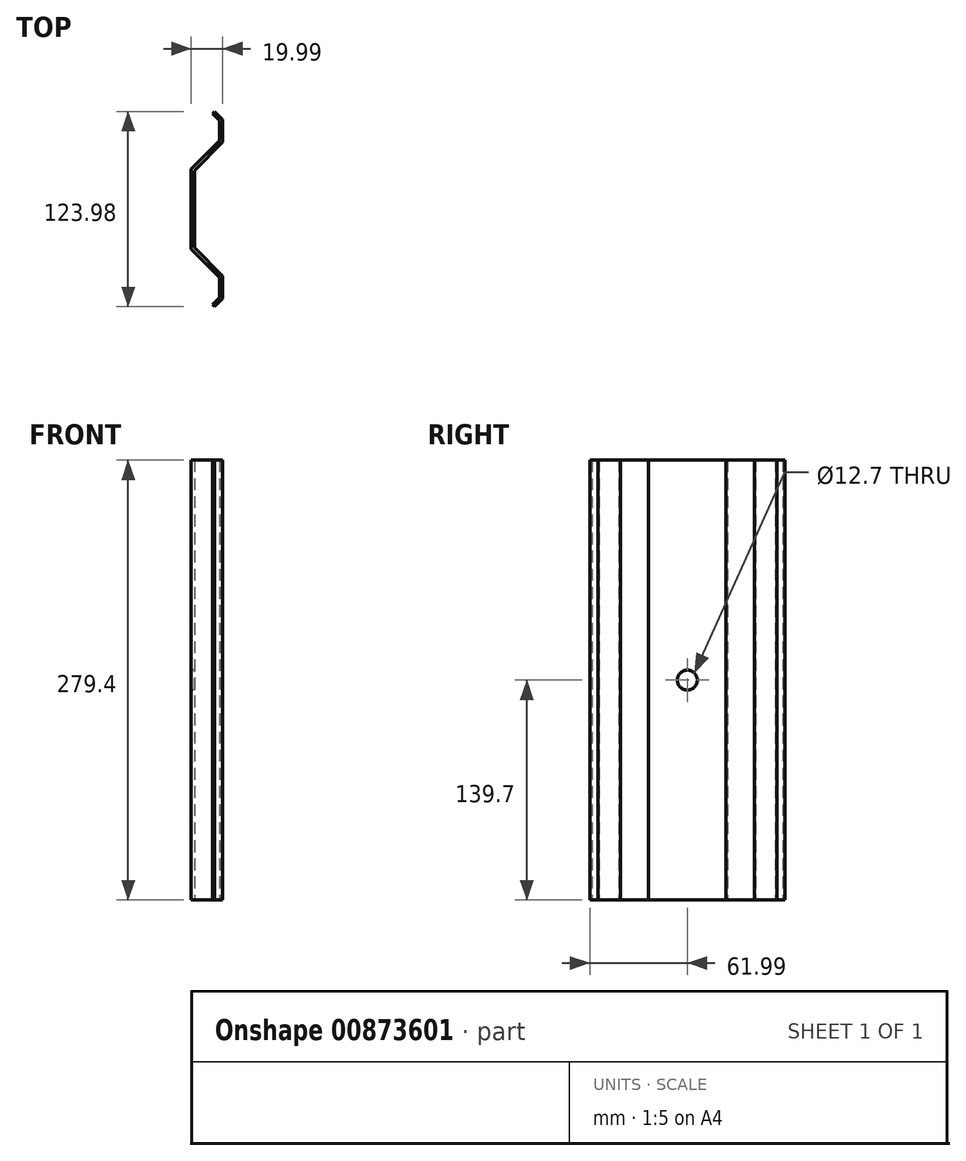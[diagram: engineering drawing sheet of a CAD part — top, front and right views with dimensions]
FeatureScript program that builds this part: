
annotation { "Feature Type Name" : "Feature", "Feature Type Description" : "" }
export const myFeature = defineFeature(function(context is Context, id is Id, definition is map)
    precondition{}
    {
        {
            var Q0;
            Q0=qCreatedBy(makeId("Top.planeOp"),FACE);
            var sketch = newSketch(context, id + "F0", { "sketchPlane" : qUnion([Q0])});
            skLineSegment(sketch, "E0", {"start": v(0, 0) * mm, "end": v(0, 25.4) * mm});
            skLineSegment(sketch, "E1", {"start": v(0, 25.4) * mm, "end": v(17.96, 43.36) * mm});
            skLineSegment(sketch, "E2", {"start": v(17.96, 43.36) * mm, "end": v(17.96, 56.06) * mm});
            skLineSegment(sketch, "E3", {"start": v(17.96, 56.06) * mm, "end": v(13.47, 60.55) * mm});
            skLineSegment(sketch, "E4.MirrorCS", {"start": v(0, 0) * mm, "end": v(0, -25.4) * mm});
            skLineSegment(sketch, "E5.MirrorCS", {"start": v(17.96, -56.06) * mm, "end": v(13.47, -60.55) * mm});
            skLineSegment(sketch, "E6.MirrorCS", {"start": v(0, -25.4) * mm, "end": v(17.96, -43.36) * mm});
            skLineSegment(sketch, "E7.MirrorCS", {"start": v(17.96, -43.36) * mm, "end": v(17.96, -56.06) * mm});
            skLineSegment(sketch, "E8.0", {"start": v(20, 56.9) * mm, "end": v(14.9, 61.99) * mm});
            skLineSegment(sketch, "E8.1", {"start": v(20, 42.52) * mm, "end": v(20, 56.9) * mm});
            skLineSegment(sketch, "E8.2", {"start": v(2.03, 24.56) * mm, "end": v(20, 42.52) * mm});
            skLineSegment(sketch, "E8.3", {"start": v(2.03, 0) * mm, "end": v(2.03, 24.56) * mm});
            skLineSegment(sketch, "E8.4", {"start": v(20, -56.9) * mm, "end": v(14.9, -61.99) * mm});
            skLineSegment(sketch, "E8.5", {"start": v(20, -42.52) * mm, "end": v(20, -56.9) * mm});
            skLineSegment(sketch, "E8.6", {"start": v(2.03, -24.56) * mm, "end": v(20, -42.52) * mm});
            skLineSegment(sketch, "E8.7", {"start": v(2.03, 0) * mm, "end": v(2.03, -24.56) * mm});
            skLineSegment(sketch, "E9", {"start": v(13.47, 60.55) * mm, "end": v(14.9, 61.99) * mm});
            skLineSegment(sketch, "E10", {"start": v(13.47, -60.55) * mm, "end": v(14.9, -61.99) * mm});
            skSolve(sketch);
        }
        {
            var Q0;
            Q0 = qSketchRegion(id + "F0", true);
            extrude(context, id + "F1", {"entities" : qUnion([Q0]), "depth" : 279.4 * mm, "offsetDistance" : 25.4 * mm});
        }
        {
            var Q0;
            Q0=makeQuery(id+"F1.opExtrude","SWEPT_FACE",FACE,{"disambiguationData":[OSD([sQuery(id+"F0.wireOp",EDGE,"E0"),sQuery(id+"F0.wireOp",EDGE,"E4.MirrorCS")])]});
            var sketch = newSketch(context, id + "F2", { "sketchPlane" : qUnion([Q0])});
            skPoint(sketch, "E11.centerSnap0", {"position": v(-25.4, 139.7) * mm});
            skCircle(sketch, "E12", {"center": v(0, 139.7) * mm, "radius": 6.35 * mm});
            skPoint(sketch, "E12.centerSnap0", {"position": v(25.4, 139.7) * mm});
            skSolve(sketch);
        }
        {
            var Q0;
            Q0 = qSketchRegion(id + "F2", true);
            extrude(context, id + "F3", {"entities" : qUnion([Q0]), "operationType" : NewBodyOperationType.REMOVE, "oppositeDirection" : true, "depth" : 25.4 * mm, "offsetDistance" : 25.4 * mm});
        }
    });
